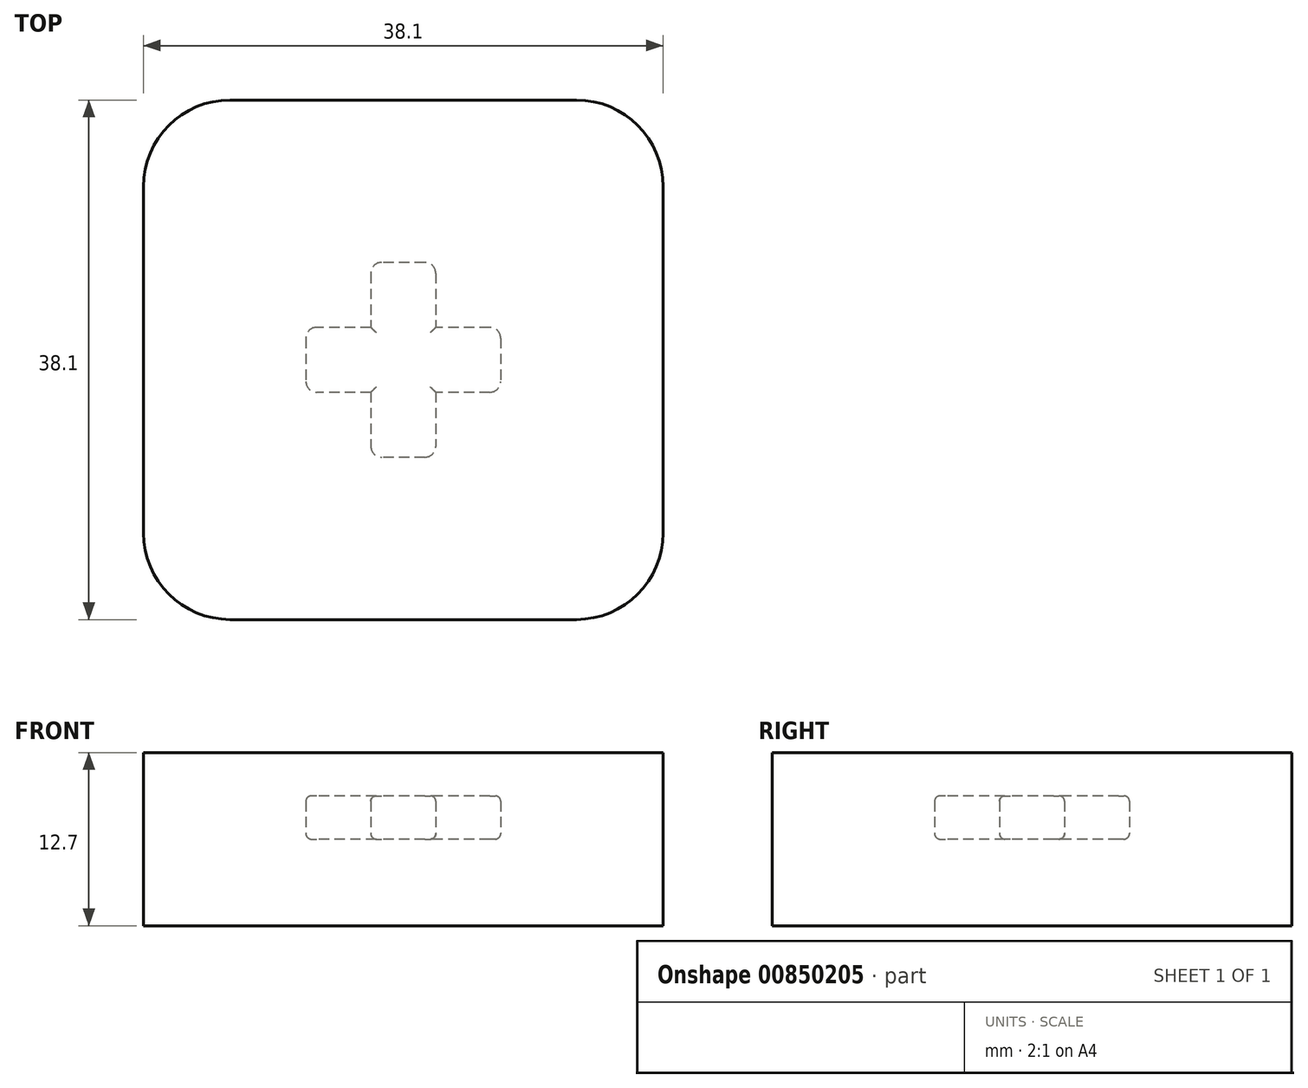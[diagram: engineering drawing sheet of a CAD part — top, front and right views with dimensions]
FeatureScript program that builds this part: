
annotation { "Feature Type Name" : "Feature", "Feature Type Description" : "" }
export const myFeature = defineFeature(function(context is Context, id is Id, definition is map)
    precondition{}
    {
        {
            var Q0;
            Q0=qCreatedBy(makeId("Top.planeOp"),FACE);
            var sketch = newSketch(context, id + "F0", { "sketchPlane" : qUnion([Q0])});
            skLineSegment(sketch, "E0.bottom", {"start": v(1.59, 7.14) * mm, "end": v(-1.59, 7.14) * mm});
            skLineSegment(sketch, "E0.top", {"start": v(1.59, -7.14) * mm, "end": v(-1.59, -7.14) * mm});
            skLineSegment(sketch, "E0.left", {"start": v(2.38, 6.35) * mm, "end": v(2.38, -6.35) * mm});
            skLineSegment(sketch, "E0.right", {"start": v(-2.38, 6.35) * mm, "end": v(-2.38, -6.35) * mm});
            skPoint(sketch, "E0.middle", {"position": v(0, 0) * mm});
            skLineSegment(sketch, "E1.bottom", {"start": v(6.35, 2.38) * mm, "end": v(-6.35, 2.38) * mm});
            skLineSegment(sketch, "E1.top", {"start": v(6.35, -2.38) * mm, "end": v(-6.35, -2.38) * mm});
            skLineSegment(sketch, "E1.left", {"start": v(7.14, 1.59) * mm, "end": v(7.14, -1.59) * mm});
            skLineSegment(sketch, "E1.right", {"start": v(-7.14, 1.59) * mm, "end": v(-7.14, -1.59) * mm});
            skPoint(sketch, "E2.visualSharp", {"position": v(-2.38, 7.14) * mm});
            skArc(sketch, "E2.filletArc", {"start": v(-1.59, 7.14) * mm, "mid": v(-2.15, 6.91) * mm, "end": v(-2.38, 6.35) * mm});
            skPoint(sketch, "E3.visualSharp", {"position": v(2.38, 7.14) * mm});
            skArc(sketch, "E3.filletArc", {"start": v(2.38, 6.35) * mm, "mid": v(2.15, 6.91) * mm, "end": v(1.59, 7.14) * mm});
            skPoint(sketch, "E4.visualSharp", {"position": v(7.14, 2.38) * mm});
            skArc(sketch, "E4.filletArc", {"start": v(7.14, 1.59) * mm, "mid": v(6.91, 2.15) * mm, "end": v(6.35, 2.38) * mm});
            skPoint(sketch, "E5.visualSharp", {"position": v(7.14, -2.38) * mm});
            skArc(sketch, "E5.filletArc", {"start": v(6.35, -2.38) * mm, "mid": v(6.91, -2.15) * mm, "end": v(7.14, -1.59) * mm});
            skPoint(sketch, "E6.visualSharp", {"position": v(2.38, -7.14) * mm});
            skArc(sketch, "E6.filletArc", {"start": v(1.59, -7.14) * mm, "mid": v(2.15, -6.91) * mm, "end": v(2.38, -6.35) * mm});
            skPoint(sketch, "E7.visualSharp", {"position": v(-2.38, -7.14) * mm});
            skArc(sketch, "E7.filletArc", {"start": v(-2.38, -6.35) * mm, "mid": v(-2.15, -6.91) * mm, "end": v(-1.59, -7.14) * mm});
            skPoint(sketch, "E8.visualSharp", {"position": v(-7.14, -2.38) * mm});
            skArc(sketch, "E8.filletArc", {"start": v(-7.14, -1.59) * mm, "mid": v(-6.91, -2.15) * mm, "end": v(-6.35, -2.38) * mm});
            skPoint(sketch, "E9.visualSharp", {"position": v(-7.14, 2.38) * mm});
            skArc(sketch, "E9.filletArc", {"start": v(-6.35, 2.38) * mm, "mid": v(-6.91, 2.15) * mm, "end": v(-7.14, 1.59) * mm});
            skSolve(sketch);
        }
        {
            var Q0;
            Q0 = qSketchRegion(id + "F0", true);
            extrude(context, id + "F1", {"entities" : qUnion([Q0]), "depth" : 3.17 * mm, "offsetDistance" : 25.4 * mm});
        }
        {
            var Q0;
            Q0=makeQuery(id+"F1.opExtrude","CAP_FACE",FACE,{"disambiguationData":[OSD([sQuery(id+"F0.wireOp",EDGE,"E0.bottom"),sQuery(id+"F0.wireOp",EDGE,"E0.top"),sQuery(id+"F0.wireOp",EDGE,"E0.left"),sQuery(id+"F0.wireOp",EDGE,"E0.right"),sQuery(id+"F0.wireOp",EDGE,"E1.bottom"),sQuery(id+"F0.wireOp",EDGE,"E1.top"),sQuery(id+"F0.wireOp",EDGE,"E1.left"),sQuery(id+"F0.wireOp",EDGE,"E1.right"),sQuery(id+"F0.wireOp",EDGE,"E2.filletArc"),sQuery(id+"F0.wireOp",EDGE,"E3.filletArc"),sQuery(id+"F0.wireOp",EDGE,"E4.filletArc"),sQuery(id+"F0.wireOp",EDGE,"E5.filletArc"),sQuery(id+"F0.wireOp",EDGE,"E6.filletArc"),sQuery(id+"F0.wireOp",EDGE,"E7.filletArc"),sQuery(id+"F0.wireOp",EDGE,"E8.filletArc"),sQuery(id+"F0.wireOp",EDGE,"E9.filletArc")])],"isStart":false});
            var Q1;
            Q1=makeQuery(id+"F1.opExtrude","CAP_FACE",FACE,{"disambiguationData":[OSD([sQuery(id+"F0.wireOp",EDGE,"E0.bottom"),sQuery(id+"F0.wireOp",EDGE,"E0.top"),sQuery(id+"F0.wireOp",EDGE,"E0.left"),sQuery(id+"F0.wireOp",EDGE,"E0.right"),sQuery(id+"F0.wireOp",EDGE,"E1.bottom"),sQuery(id+"F0.wireOp",EDGE,"E1.top"),sQuery(id+"F0.wireOp",EDGE,"E1.left"),sQuery(id+"F0.wireOp",EDGE,"E1.right"),sQuery(id+"F0.wireOp",EDGE,"E2.filletArc"),sQuery(id+"F0.wireOp",EDGE,"E3.filletArc"),sQuery(id+"F0.wireOp",EDGE,"E4.filletArc"),sQuery(id+"F0.wireOp",EDGE,"E5.filletArc"),sQuery(id+"F0.wireOp",EDGE,"E6.filletArc"),sQuery(id+"F0.wireOp",EDGE,"E7.filletArc"),sQuery(id+"F0.wireOp",EDGE,"E8.filletArc"),sQuery(id+"F0.wireOp",EDGE,"E9.filletArc")])],"isStart":true});
            fillet(context, id + "F2", {"entities" : qUnion([Q0, Q1]), "tangentPropagation" : true, "radius" : 0.4 * mm, "defaultsChanged" : false, "vertexSettings" : [], "allowEdgeOverflow" : false});
        }
        {
            var Q0;
            Q0=qCreatedBy(makeId("Top.planeOp"),FACE);
            cPlane(context, id + "F3", {"entities" : qUnion([Q0]), "cplaneType" : CPlaneType.OFFSET, "offset" : 1 / 406.4 * mm, "width" : 152.4 * mm, "height" : 152.4 * mm});
        }
        {
            var Q0;
            Q0=qCreatedBy(id+"F3.planeOp",FACE);
            var sketch = newSketch(context, id + "F4", { "sketchPlane" : qUnion([Q0])});
            skLineSegment(sketch, "E10.bottom", {"start": v(12.7, 19.05) * mm, "end": v(-12.7, 19.05) * mm});
            skLineSegment(sketch, "E10.top", {"start": v(12.7, -19.05) * mm, "end": v(-12.7, -19.05) * mm});
            skLineSegment(sketch, "E10.left", {"start": v(19.05, 12.7) * mm, "end": v(19.05, -12.7) * mm});
            skLineSegment(sketch, "E10.right", {"start": v(-19.05, 12.7) * mm, "end": v(-19.05, -12.7) * mm});
            skPoint(sketch, "E10.middle", {"position": v(0, 0) * mm});
            skPoint(sketch, "E11.visualSharp", {"position": v(-19.05, 19.05) * mm});
            skArc(sketch, "E11.filletArc", {"start": v(-12.7, 19.05) * mm, "mid": v(-17.2, 17.2) * mm, "end": v(-19.05, 12.7) * mm});
            skPoint(sketch, "E12.visualSharp", {"position": v(19.05, 19.05) * mm});
            skArc(sketch, "E12.filletArc", {"start": v(19.05, 12.7) * mm, "mid": v(17.2, 17.2) * mm, "end": v(12.7, 19.05) * mm});
            skPoint(sketch, "E13.visualSharp", {"position": v(19.05, -19.05) * mm});
            skArc(sketch, "E13.filletArc", {"start": v(12.7, -19.05) * mm, "mid": v(17.2, -17.2) * mm, "end": v(19.05, -12.7) * mm});
            skPoint(sketch, "E14.visualSharp", {"position": v(-19.05, -19.05) * mm});
            skArc(sketch, "E14.filletArc", {"start": v(-19.05, -12.7) * mm, "mid": v(-17.2, -17.2) * mm, "end": v(-12.7, -19.05) * mm});
            skSolve(sketch);
        }
        {
            var Q0;
            Q0 = qSketchRegion(id + "F4", true);
            extrude(context, id + "F5", {"entities" : qUnion([Q0]), "depth" : 6.35 * mm, "offsetDistance" : 25.4 * mm, "hasSecondDirection" : true, "secondDirectionOppositeDirection" : true, "secondDirectionDepth" : 6.35 * mm});
        }
    });
